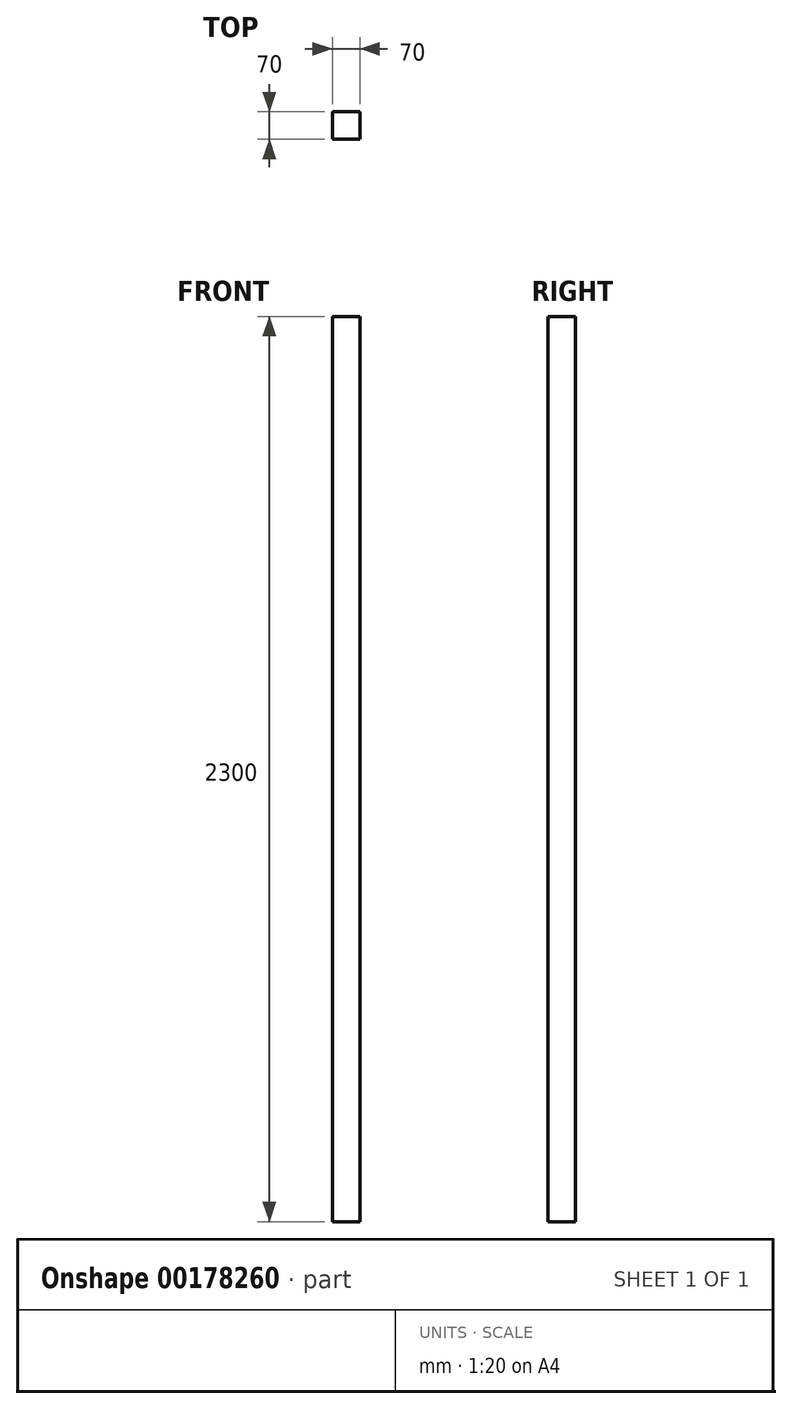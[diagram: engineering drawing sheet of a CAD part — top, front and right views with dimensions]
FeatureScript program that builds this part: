
annotation { "Feature Type Name" : "Feature", "Feature Type Description" : "" }
export const myFeature = defineFeature(function(context is Context, id is Id, definition is map)
    precondition{}
    {
        {
            var Q0;
            Q0=qCreatedBy(makeId("Top.planeOp"),FACE);
            var sketch = newSketch(context, id + "F0", { "sketchPlane" : qUnion([Q0])});
            skLineSegment(sketch, "E0.bottom", {"start": v(-35, -35) * mm, "end": v(35, -35) * mm});
            skLineSegment(sketch, "E0.top", {"start": v(-35, 35) * mm, "end": v(35, 35) * mm});
            skLineSegment(sketch, "E0.left", {"start": v(-35, -35) * mm, "end": v(-35, 35) * mm});
            skLineSegment(sketch, "E0.right", {"start": v(35, -35) * mm, "end": v(35, 35) * mm});
            skPoint(sketch, "E0.middle", {"position": v(0, 0) * mm});
            skSolve(sketch);
        }
        {
            var Q0;
            Q0 = qSketchRegion(id + "F0", true);
            extrude(context, id + "F1", {"entities" : qUnion([Q0]), "depth" : 2300 * mm});
        }
    });
